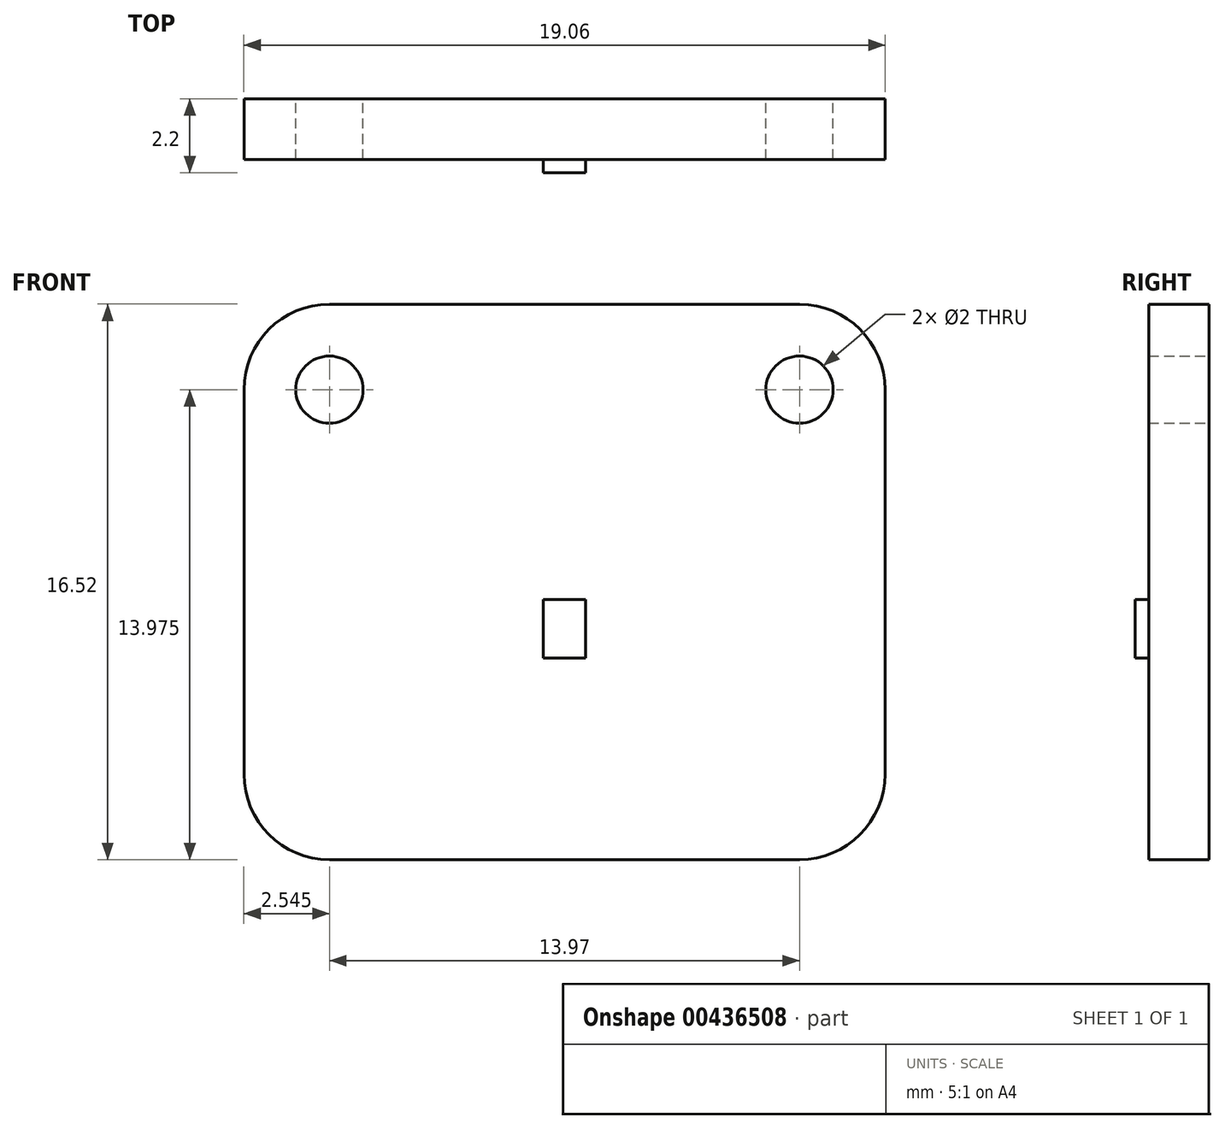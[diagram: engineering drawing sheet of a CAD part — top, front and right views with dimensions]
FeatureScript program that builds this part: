
annotation { "Feature Type Name" : "Feature", "Feature Type Description" : "" }
export const myFeature = defineFeature(function(context is Context, id is Id, definition is map)
    precondition{}
    {
        {
            var Q0;
            Q0=qCreatedBy(makeId("Front.planeOp"),FACE);
            var sketch = newSketch(context, id + "F0", { "sketchPlane" : qUnion([Q0])});
            skLineSegment(sketch, "E0.bottom", {"start": v(9.52, 8.26) * mm, "end": v(-9.53, 8.26) * mm});
            skLineSegment(sketch, "E0.top", {"start": v(9.53, -8.26) * mm, "end": v(-9.52, -8.26) * mm});
            skLineSegment(sketch, "E0.left", {"start": v(9.52, 8.26) * mm, "end": v(9.53, -8.26) * mm});
            skLineSegment(sketch, "E0.right", {"start": v(-9.53, 8.26) * mm, "end": v(-9.52, -8.26) * mm});
            skPoint(sketch, "E0.middle", {"position": v(0, 0) * mm});
            skCircle(sketch, "E1", {"center": v(-6.99, 5.71) * mm, "radius": 1 * mm});
            skCircle(sketch, "E2", {"center": v(6.98, 5.72) * mm, "radius": 1 * mm});
            skLineSegment(sketch, "E3.bottom", {"start": v(0.62, -0.53) * mm, "end": v(-0.62, -0.53) * mm});
            skLineSegment(sketch, "E3.top", {"start": v(0.62, -2.27) * mm, "end": v(-0.63, -2.27) * mm});
            skLineSegment(sketch, "E3.left", {"start": v(0.63, -0.53) * mm, "end": v(0.62, -2.27) * mm});
            skLineSegment(sketch, "E3.right", {"start": v(-0.62, -0.53) * mm, "end": v(-0.63, -2.27) * mm});
            skPoint(sketch, "E3.middle", {"position": v(0, -1.4) * mm});
            skSolve(sketch);
        }
        {
            var Q0;
            Q0=makeQuery(id+"F0.imprint","IMPRINT",FACE,{"disambiguationData":[TD([[makeQuery(id+"F0.imprint","IMPRINT",EDGE,{"derivedFrom":sQuery(id+"F0.wireOp",EDGE,"E0.bottom")}),1.0]])]});
            extrude(context, id + "F1", {"entities" : qUnion([Q0]), "depth" : 1.8 * mm});
        }
        {
            var Q0;
            Q0=makeQuery(id+"F0.imprint","IMPRINT",FACE,{"disambiguationData":[TD([[makeQuery(id+"F0.imprint","IMPRINT",EDGE,{"derivedFrom":sQuery(id+"F0.wireOp",EDGE,"E3.bottom")}),1.0]])]});
            extrude(context, id + "F2", {"entities" : qUnion([Q0]), "operationType" : NewBodyOperationType.ADD, "depth" : 2.2 * mm});
        }
        {
            var Q0;
            Q0=makeQuery(id+"F1.opExtrude","SWEPT_EDGE",EDGE,{"disambiguationData":[OSD([sQuery(id+"F0.wireOp",EDGE,"E0.bottom"),sQuery(id+"F0.wireOp",EDGE,"E0.right")])]});
            var Q1;
            Q1=makeQuery(id+"F1.opExtrude","SWEPT_EDGE",EDGE,{"disambiguationData":[OSD([sQuery(id+"F0.wireOp",EDGE,"E0.bottom"),sQuery(id+"F0.wireOp",EDGE,"E0.left")])]});
            var Q2;
            Q2=makeQuery(id+"F1.opExtrude","SWEPT_EDGE",EDGE,{"disambiguationData":[OSD([sQuery(id+"F0.wireOp",EDGE,"E0.top"),sQuery(id+"F0.wireOp",EDGE,"E0.left")])]});
            var Q3;
            Q3=makeQuery(id+"F1.opExtrude","SWEPT_EDGE",EDGE,{"disambiguationData":[OSD([sQuery(id+"F0.wireOp",EDGE,"E0.top"),sQuery(id+"F0.wireOp",EDGE,"E0.right")])]});
            fillet(context, id + "F3", {"entities" : qUnion([Q0, Q1, Q2, Q3]), "radius" : 2.54 * mm, "tangentPropagation" : true, "allowEdgeOverflow" : false});
        }
    });
